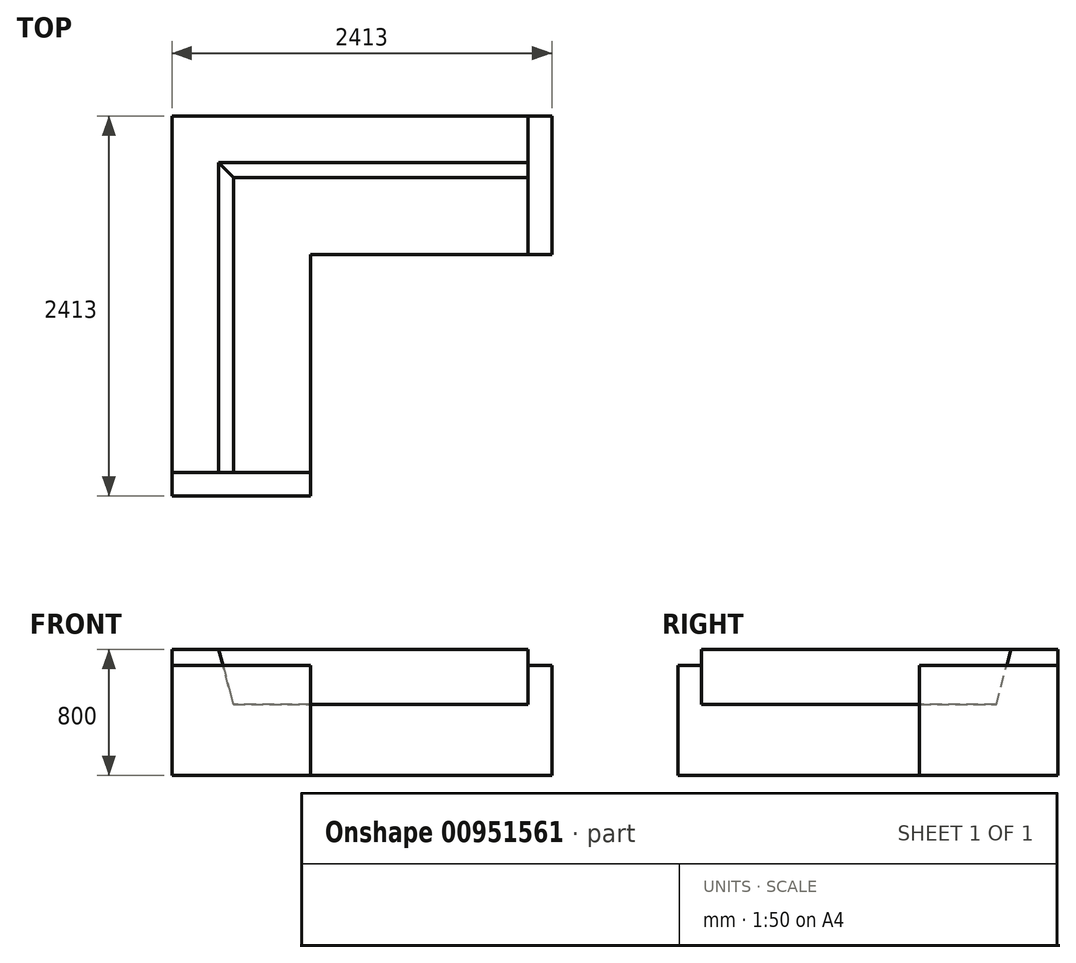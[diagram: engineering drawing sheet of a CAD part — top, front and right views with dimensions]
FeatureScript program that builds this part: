
annotation { "Feature Type Name" : "Feature", "Feature Type Description" : "" }
export const myFeature = defineFeature(function(context is Context, id is Id, definition is map)
    precondition{}
    {
        {
            var Q0;
            Q0=qCreatedBy(makeId("Top.planeOp"),FACE);
            var sketch = newSketch(context, id + "F0", { "sketchPlane" : qUnion([Q0])});
            skLineSegment(sketch, "E0", {"start": v(0, 0) * mm, "end": v(0, 2413) * mm});
            skLineSegment(sketch, "E1", {"start": v(0, 2413) * mm, "end": v(2413, 2413) * mm});
            skLineSegment(sketch, "E2", {"start": v(0, 0) * mm, "end": v(879.48, 0) * mm});
            skLineSegment(sketch, "E3", {"start": v(2413, 2413) * mm, "end": v(2413, 1533.53) * mm});
            skLineSegment(sketch, "E4", {"start": v(879.48, 0) * mm, "end": v(879.48, 1533.53) * mm});
            skLineSegment(sketch, "E5", {"start": v(879.48, 1533.53) * mm, "end": v(2413, 1533.53) * mm});
            skSolve(sketch);
        }
        {
            var Q0;
            Q0=qSketchRegion(id+"F0",true);
            extrude(context, id + "F1", {"entities" : qUnion([Q0]), "depth" : 450 * mm, "offsetDistance" : 25.4 * mm});
        }
        {
            var Q0;
            Q0=makeQuery(id+"F1.opExtrude","CAP_FACE",FACE,{"disambiguationData":[OSD([sQuery(id+"F0.wireOp",EDGE,"E0"),sQuery(id+"F0.wireOp",EDGE,"E1"),sQuery(id+"F0.wireOp",EDGE,"E2"),sQuery(id+"F0.wireOp",EDGE,"E3"),sQuery(id+"F0.wireOp",EDGE,"E4"),sQuery(id+"F0.wireOp",EDGE,"E5")])],"isStart":false});
            var sketch = newSketch(context, id + "F2", { "sketchPlane" : qUnion([Q0])});
            skLineSegment(sketch, "E6.bottom", {"start": v(879.48, 0) * mm, "end": v(0, 0) * mm});
            skLineSegment(sketch, "E6.top", {"start": v(879.48, 150) * mm, "end": v(0, 150) * mm});
            skLineSegment(sketch, "E6.left", {"start": v(879.48, 0) * mm, "end": v(879.48, 150) * mm});
            skLineSegment(sketch, "E6.right", {"start": v(0, 0) * mm, "end": v(0, 150) * mm});
            skLineSegment(sketch, "E7.bottom", {"start": v(2413, 1533.53) * mm, "end": v(2263, 1533.53) * mm});
            skLineSegment(sketch, "E7.top", {"start": v(2413, 2413) * mm, "end": v(2263, 2413) * mm});
            skLineSegment(sketch, "E7.left", {"start": v(2413, 1533.53) * mm, "end": v(2413, 2413) * mm});
            skLineSegment(sketch, "E7.right", {"start": v(2263, 1533.53) * mm, "end": v(2263, 2413) * mm});
            skSolve(sketch);
        }
        {
            var Q0;
            Q0=qSketchRegion(id+"F2",true);
            extrude(context, id + "F3", {"entities" : qUnion([Q0]), "operationType" : NewBodyOperationType.ADD, "depth" : 700 * mm - 450 * mm, "offsetDistance" : 25.4 * mm});
        }
        {
            var Q0;
            Q0=makeQuery(id+"F3.opExtrude","SWEPT_FACE",FACE,{"disambiguationData":[OSD([sQuery(id+"F2.wireOp",EDGE,"E6.top")])]});
            var sketch = newSketch(context, id + "F4", { "sketchPlane" : qUnion([Q0])});
            skLineSegment(sketch, "E8", {"start": v(0, 450) * mm, "end": v(0, 800) * mm});
            skLineSegment(sketch, "E9", {"start": v(0, 800) * mm, "end": v(-296.74, 800) * mm});
            skLineSegment(sketch, "E10", {"start": v(-296.74, 800) * mm, "end": v(-390.52, 450) * mm});
            skLineSegment(sketch, "E11", {"start": v(-390.52, 450) * mm, "end": v(0, 450) * mm});
            skSolve(sketch);
        }
        {
            var Q0;
            Q0=qSketchRegion(id+"F4",true);
            var Q1;
            Q1=makeQuery(id+"F3.boolean.opBoolean","MERGE",FACE,{"derivedFrom":[makeQuery(id+"F1.opExtrude","SWEPT_FACE",FACE,{"disambiguationData":[OSD([sQuery(id+"F0.wireOp",EDGE,"E1")])]}),makeQuery(id+"F3.opExtrude","SWEPT_FACE",FACE,{"disambiguationData":[OSD([sQuery(id+"F2.wireOp",EDGE,"E7.top")])]})]});
            extrude(context, id + "F5", {"entities" : qUnion([Q0]), "operationType" : NewBodyOperationType.ADD, "endBound" : BoundingType.UP_TO_SURFACE, "depth" : 25.4 * mm, "endBoundEntityFace" : qUnion([Q1]), "offsetDistance" : 25.4 * mm});
        }
        {
            var Q0;
            Q0=makeQuery(id+"F3.opExtrude","SWEPT_FACE",FACE,{"disambiguationData":[OSD([sQuery(id+"F2.wireOp",EDGE,"E7.right")])]});
            var sketch = newSketch(context, id + "F6", { "sketchPlane" : qUnion([Q0])});
            skLineSegment(sketch, "E12", {"start": v(-2413, 450) * mm, "end": v(-2022.47, 450) * mm});
            skLineSegment(sketch, "E13", {"start": v(-2022.47, 450) * mm, "end": v(-2116.26, 800) * mm});
            skLineSegment(sketch, "E14", {"start": v(-2116.26, 800) * mm, "end": v(-2413, 800) * mm});
            skLineSegment(sketch, "E15", {"start": v(-2413, 800) * mm, "end": v(-2413, 450) * mm});
            skSolve(sketch);
        }
        {
            var Q0;
            Q0=qSketchRegion(id+"F6",true);
            extrude(context, id + "F7", {"entities" : qUnion([Q0]), "operationType" : NewBodyOperationType.ADD, "endBound" : BoundingType.UP_TO_NEXT, "depth" : 25.4 * mm, "offsetDistance" : 25.4 * mm});
        }
    });
